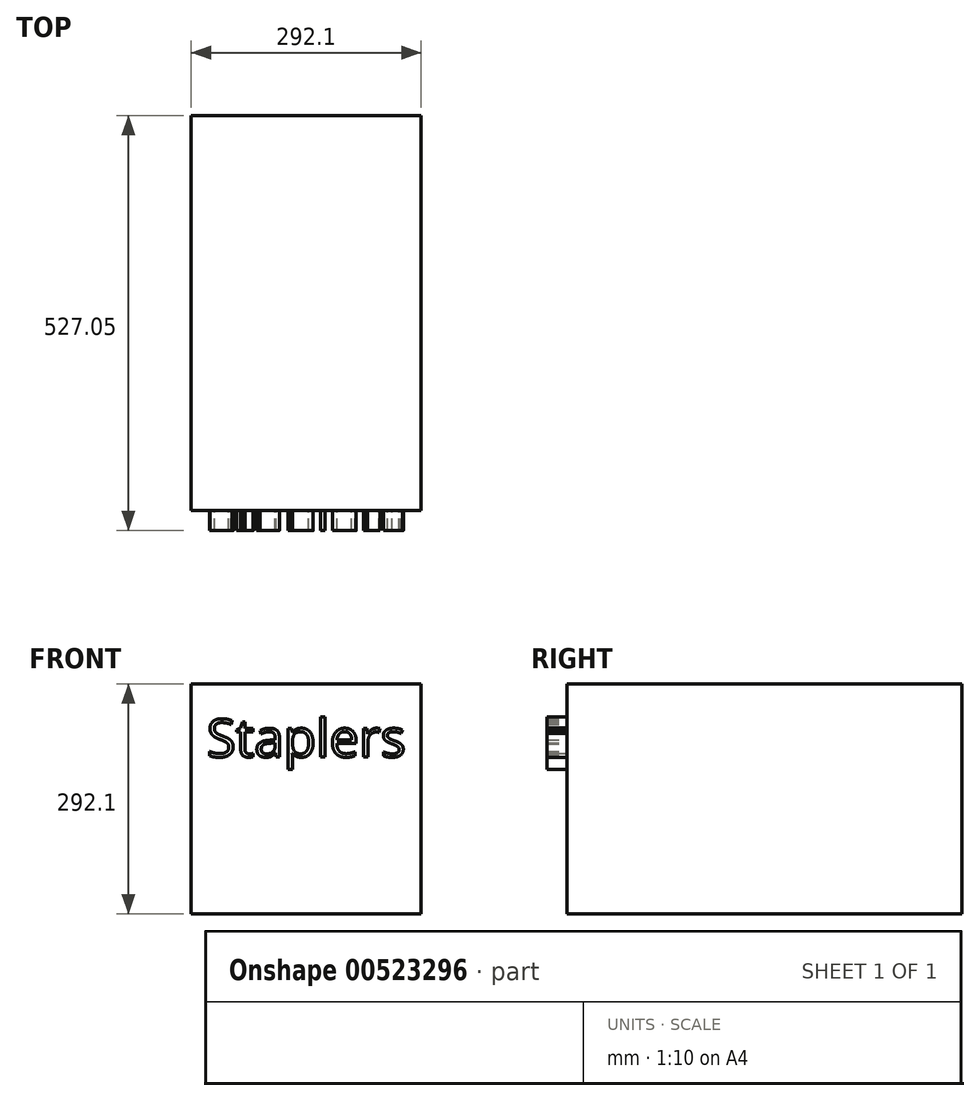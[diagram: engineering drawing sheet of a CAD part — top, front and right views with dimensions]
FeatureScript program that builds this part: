
annotation { "Feature Type Name" : "Feature", "Feature Type Description" : "" }
export const myFeature = defineFeature(function(context is Context, id is Id, definition is map)
    precondition{}
    {
        {
            var Q0;
            Q0=qCreatedBy(makeId("Front.planeOp"),FACE);
            var sketch = newSketch(context, id + "F0", { "sketchPlane" : qUnion([Q0])});
            skLineSegment(sketch, "E0.bottom", {"start": v(146.05, 146.05) * mm, "end": v(-146.05, 146.05) * mm});
            skLineSegment(sketch, "E0.top", {"start": v(146.05, -146.05) * mm, "end": v(-146.05, -146.05) * mm});
            skLineSegment(sketch, "E0.left", {"start": v(146.05, 146.05) * mm, "end": v(146.05, -146.05) * mm});
            skLineSegment(sketch, "E0.right", {"start": v(-146.05, 146.05) * mm, "end": v(-146.05, -146.05) * mm});
            skPoint(sketch, "E0.middle", {"position": v(0, 0) * mm});
            skSolve(sketch);
        }
        {
            var Q0;
            Q0=makeQuery(id+"F0.imprint","IMPRINT",FACE,{"disambiguationData":[TD([[makeQuery(id+"F0.imprint","IMPRINT",EDGE,{"derivedFrom":sQuery(id+"F0.wireOp",EDGE,"E0.bottom")}),1.0]])]});
            extrude(context, id + "F1", {"entities" : qUnion([Q0]), "depth" : 501.65 * mm, "offsetDistance" : 25.4 * mm});
        }
        {
            var Q0;
            Q0=makeQuery(id+"F1.opExtrude","CAP_FACE",FACE,{"disambiguationData":[OSD([sQuery(id+"F0.wireOp",EDGE,"E0.bottom"),sQuery(id+"F0.wireOp",EDGE,"E0.top"),sQuery(id+"F0.wireOp",EDGE,"E0.left"),sQuery(id+"F0.wireOp",EDGE,"E0.right")])],"isStart":false});
            var sketch = newSketch(context, id + "F2", { "sketchPlane" : qUnion([Q0])});
            skText(sketch, "E1", { "text": "Staplers", "fontName": "OpenSans-Regular.ttf"});
            const initialGuessF2  = {"E1": [-0.12643, 0.05341, 1, 0, 0.04827]};
            skSetInitialGuess(sketch, initialGuessF2);
            skSolve(sketch);
        }
        {
            var Q0;
            Q0 = qSketchRegion(id + "F2", true);
            extrude(context, id + "F3", {"entities" : qUnion([Q0]), "operationType" : NewBodyOperationType.ADD, "depth" : 25.4 * mm, "offsetDistance" : 25.4 * mm});
        }
    });
